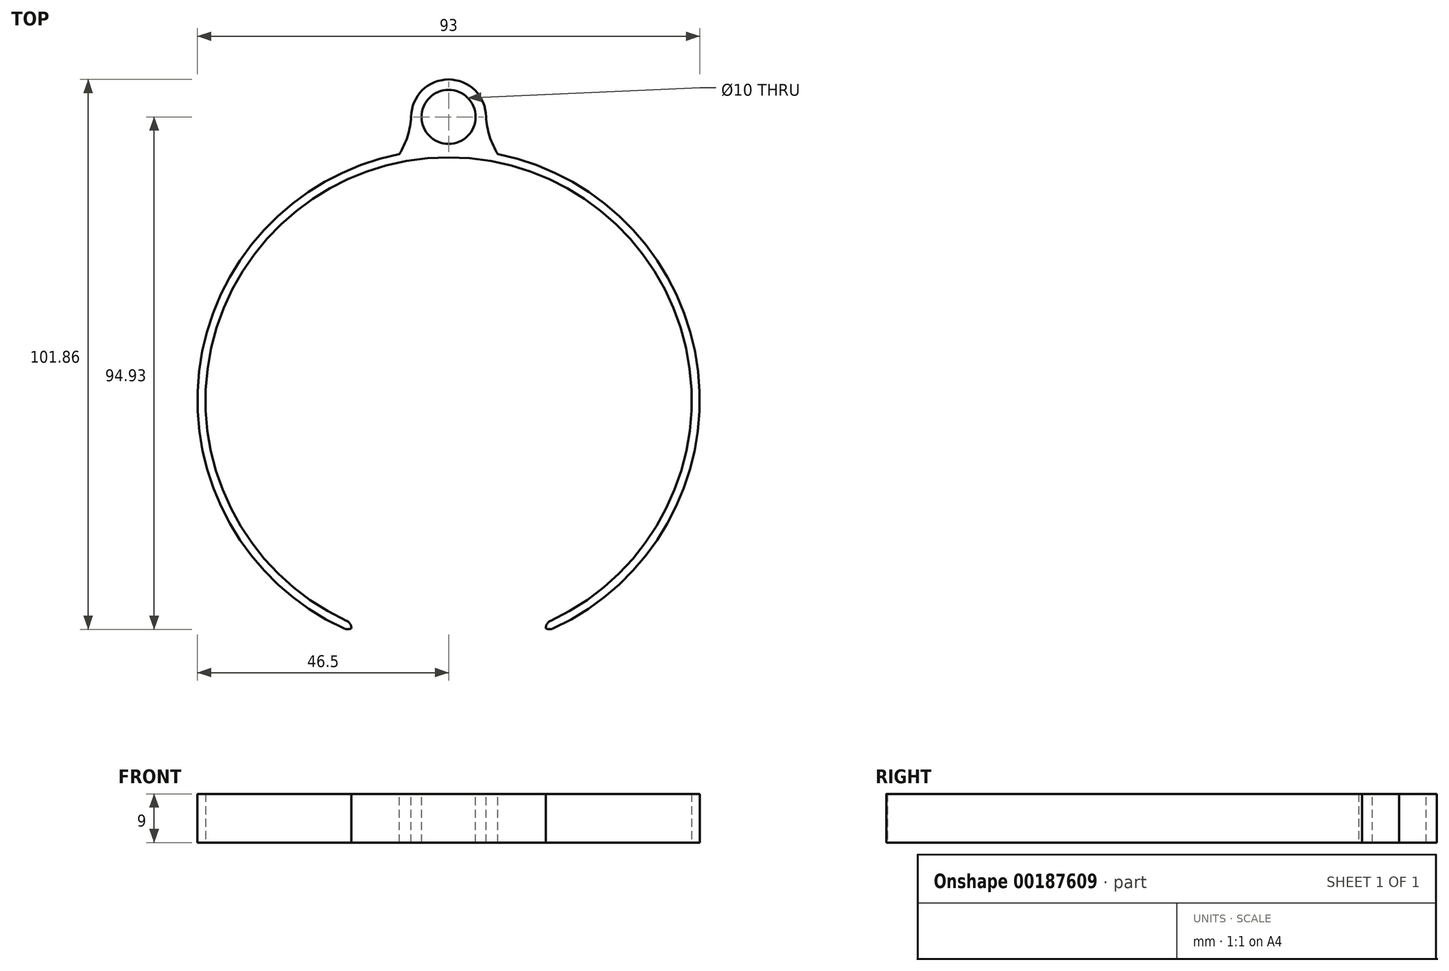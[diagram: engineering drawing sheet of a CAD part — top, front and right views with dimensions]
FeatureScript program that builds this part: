
annotation { "Feature Type Name" : "Feature", "Feature Type Description" : "" }
export const myFeature = defineFeature(function(context is Context, id is Id, definition is map)
    precondition{}
    {
        {
            var Q0;
            Q0=qCreatedBy(makeId("Top.planeOp"),FACE);
            var sketch = newSketch(context, id + "F0", { "sketchPlane" : qUnion([Q0])});
            skCircle(sketch, "E0", {"center": v(0, 0) * mm, "radius": 46.5 * mm});
            skCircle(sketch, "E1", {"center": v(0, 0) * mm, "radius": 45 * mm});
            skSolve(sketch);
        }
        {
            var Q0;
            Q0 = qSketchRegion(id + "F0", true);
            extrude(context, id + "F1", {"entities" : qUnion([Q0]), "depth" : 9 * mm});
        }
        {
            var Q0;
            Q0=makeQuery(id+"F1.opExtrude","CAP_FACE",FACE,{"disambiguationData":[OSD([sQuery(id+"F0.wireOp",EDGE,"E0"),sQuery(id+"F0.wireOp",EDGE,"E1")])],"isStart":false});
            var sketch = newSketch(context, id + "F2", { "sketchPlane" : qUnion([Q0])});
            skLineSegment(sketch, "E2", {"start": v(0, -21.51) * mm, "end": v(-51.57, -21.51) * mm});
            skLineSegment(sketch, "E3", {"start": v(-51.57, -21.51) * mm, "end": v(-51.57, -59.92) * mm});
            skLineSegment(sketch, "E4", {"start": v(-51.57, -59.92) * mm, "end": v(64.03, -57.77) * mm});
            skLineSegment(sketch, "E5", {"start": v(0, -21.51) * mm, "end": v(64.81, -21.51) * mm});
            skLineSegment(sketch, "E6", {"start": v(64.81, -21.51) * mm, "end": v(64.03, -57.77) * mm});
            skSolve(sketch);
        }
        {
            var Q0;
            Q0 = qSketchRegion(id + "F2", true);
            extrude(context, id + "F3", {"entities" : qUnion([Q0]), "operationType" : NewBodyOperationType.REMOVE, "oppositeDirection" : true, "depth" : 25 * mm});
        }
        {
            var Q0;
            Q0=makeQuery(id+"F1.opExtrude","CAP_FACE",FACE,{"disambiguationData":[OSD([sQuery(id+"F0.wireOp",EDGE,"E0"),sQuery(id+"F0.wireOp",EDGE,"E1")])],"isStart":false});
            var sketch = newSketch(context, id + "F4", { "sketchPlane" : qUnion([Q0])});
            skArc(sketch, "E7", {"start": v(-41.9, -20.16) * mm, "mid": v(-40.9, -20.5) * mm, "end": v(-40.55, -19.5) * mm});
            skLineSegment(sketch, "E8", {"start": v(-41.9, -20.16) * mm, "end": v(-43.43, -22.72) * mm});
            skLineSegment(sketch, "E9", {"start": v(-43.43, -22.72) * mm, "end": v(-36.35, -23.45) * mm});
            skLineSegment(sketch, "E10", {"start": v(-36.35, -23.45) * mm, "end": v(-40.55, -19.5) * mm});
            skLineSegment(sketch, "E11", {"start": v(0, 0) * mm, "end": v(0, -21.51) * mm});
            skArc(sketch, "E12.MirrorCS", {"start": v(41.9, -20.16) * mm, "mid": v(40.9, -20.5) * mm, "end": v(40.55, -19.5) * mm});
            skLineSegment(sketch, "E13.MirrorCS", {"start": v(36.35, -23.45) * mm, "end": v(40.55, -19.5) * mm});
            skLineSegment(sketch, "E14.MirrorCS", {"start": v(43.43, -22.72) * mm, "end": v(36.35, -23.45) * mm});
            skLineSegment(sketch, "E15.MirrorCS", {"start": v(41.9, -20.16) * mm, "end": v(43.43, -22.72) * mm});
            skSolve(sketch);
        }
        {
            var Q0;
            Q0 = qSketchRegion(id + "F4", true);
            extrude(context, id + "F5", {"entities" : qUnion([Q0]), "operationType" : NewBodyOperationType.REMOVE, "oppositeDirection" : true, "depth" : 25 * mm});
        }
        {
            var Q0;
            Q0=makeQuery(id+"F1.opExtrude","CAP_FACE",FACE,{"disambiguationData":[OSD([sQuery(id+"F0.wireOp",EDGE,"E0"),sQuery(id+"F0.wireOp",EDGE,"E1")])],"isStart":false});
            var sketch = newSketch(context, id + "F6", { "sketchPlane" : qUnion([Q0])});
            skLineSegment(sketch, "E16", {"start": v(0, 0) * mm, "end": v(0, 52.5) * mm});
            skCircle(sketch, "E17", {"center": v(0, 52.5) * mm, "radius": 5 * mm});
            skCircle(sketch, "E18", {"center": v(0, 52.5) * mm, "radius": 6.93 * mm});
            skSolve(sketch);
        }
        {
            var Q0;
            Q0 = qSketchRegion(id + "F6", true);
            extrude(context, id + "F7", {"entities" : qUnion([Q0]), "operationType" : NewBodyOperationType.ADD, "oppositeDirection" : true, "depth" : 9 * mm});
        }
        {
            var Q0;
            Q0=makeQuery(id+"F7.boolean.opBoolean","MERGE",FACE,{"derivedFrom":[makeQuery(id+"F1.opExtrude","CAP_FACE",FACE,{"disambiguationData":[OSD([sQuery(id+"F0.wireOp",EDGE,"E0"),sQuery(id+"F0.wireOp",EDGE,"E1")])],"isStart":false}),makeQuery(id+"F7.opExtrude","CAP_FACE",FACE,{"disambiguationData":[OSD([sQuery(id+"F6.wireOp",EDGE,"E17"),sQuery(id+"F6.wireOp",EDGE,"E18")])],"isStart":true})]});
            var sketch = newSketch(context, id + "F8", { "sketchPlane" : qUnion([Q0])});
            skArc(sketch, "E19", {"start": v(-9.12, 45.6) * mm, "mid": v(-7.6, 48.91) * mm, "end": v(-6.93, 52.5) * mm});
            skArc(sketch, "E20.MirrorCS", {"start": v(9.12, 45.6) * mm, "mid": v(7.6, 48.91) * mm, "end": v(6.93, 52.5) * mm});
            skArc(sketch, "E21", {"start": v(9.12, 45.6) * mm, "mid": v(0, 45.6) * mm, "end": v(-9.12, 45.6) * mm});
            skArc(sketch, "E22", {"start": v(-6.93, 52.5) * mm, "mid": v(0, 47) * mm, "end": v(6.93, 52.5) * mm});
            skSolve(sketch);
        }
        {
            var Q0;
            Q0 = qSketchRegion(id + "F8", true);
            extrude(context, id + "F9", {"entities" : qUnion([Q0]), "operationType" : NewBodyOperationType.ADD, "oppositeDirection" : true, "depth" : 9 * mm});
        }
        {
            var Q0;
            Q0=makeQuery(id+"F9.boolean.opBoolean","MERGE",FACE,{"derivedFrom":[makeQuery(id+"F7.boolean.opBoolean","MERGE",FACE,{"derivedFrom":[makeQuery(id+"F1.opExtrude","CAP_FACE",FACE,{"disambiguationData":[OSD([sQuery(id+"F0.wireOp",EDGE,"E0"),sQuery(id+"F0.wireOp",EDGE,"E1")])],"isStart":false}),makeQuery(id+"F7.opExtrude","CAP_FACE",FACE,{"disambiguationData":[OSD([sQuery(id+"F6.wireOp",EDGE,"E17"),sQuery(id+"F6.wireOp",EDGE,"E18")])],"isStart":true})]}),makeQuery(id+"F9.opExtrude","CAP_FACE",FACE,{"disambiguationData":[OSD([sQuery(id+"F8.wireOp",EDGE,"E19"),sQuery(id+"F8.wireOp",EDGE,"E20.MirrorCS"),sQuery(id+"F8.wireOp",EDGE,"E21"),sQuery(id+"F8.wireOp",EDGE,"E22")])],"isStart":true})]});
            var sketch = newSketch(context, id + "F10", { "sketchPlane" : qUnion([Q0])});
            skArc(sketch, "E23", {"start": v(-46.35, 3.8) * mm, "mid": v(-42.8, -9.52) * mm, "end": v(-33.84, -20) * mm});
            skArc(sketch, "E24", {"start": v(-44.83, 3.9) * mm, "mid": v(-41.28, -9.32) * mm, "end": v(-32.15, -19.5) * mm});
            skArc(sketch, "E25", {"start": v(-33.84, -20) * mm, "mid": v(-32.86, -20.21) * mm, "end": v(-32.15, -19.5) * mm});
            skLineSegment(sketch, "E26", {"start": v(-46.35, 3.8) * mm, "end": v(-44.83, 3.9) * mm});
            skLineSegment(sketch, "E27", {"start": v(0, 0) * mm, "end": v(0, 28.55) * mm});
            skLineSegment(sketch, "E28.MirrorCS", {"start": v(46.35, 3.8) * mm, "end": v(44.83, 3.9) * mm});
            skArc(sketch, "E29.MirrorCS", {"start": v(46.35, 3.8) * mm, "mid": v(42.8, -9.52) * mm, "end": v(33.84, -20) * mm});
            skArc(sketch, "E30.MirrorCS", {"start": v(44.83, 3.9) * mm, "mid": v(41.28, -9.32) * mm, "end": v(32.15, -19.5) * mm});
            skArc(sketch, "E31.MirrorCS", {"start": v(33.84, -20) * mm, "mid": v(32.86, -20.21) * mm, "end": v(32.15, -19.5) * mm});
            skSolve(sketch);
        }
        {
            var Q0;
            Q0 = qSketchRegion(id + "F10", true);
            extrude(context, id + "F11", {"entities" : qUnion([Q0]), "operationType" : NewBodyOperationType.ADD, "oppositeDirection" : true, "depth" : 9 * mm});
        }
        {
            var Q0;
            Q0=makeQuery(id+"F11.boolean.opBoolean","MERGE",FACE,{"derivedFrom":[makeQuery(id+"F9.boolean.opBoolean","MERGE",FACE,{"derivedFrom":[makeQuery(id+"F7.boolean.opBoolean","MERGE",FACE,{"derivedFrom":[makeQuery(id+"F1.opExtrude","CAP_FACE",FACE,{"disambiguationData":[OSD([sQuery(id+"F0.wireOp",EDGE,"E0"),sQuery(id+"F0.wireOp",EDGE,"E1")])],"isStart":false}),makeQuery(id+"F7.opExtrude","CAP_FACE",FACE,{"disambiguationData":[OSD([sQuery(id+"F6.wireOp",EDGE,"E17"),sQuery(id+"F6.wireOp",EDGE,"E18")])],"isStart":true})]}),makeQuery(id+"F9.opExtrude","CAP_FACE",FACE,{"disambiguationData":[OSD([sQuery(id+"F8.wireOp",EDGE,"E19"),sQuery(id+"F8.wireOp",EDGE,"E20.MirrorCS"),sQuery(id+"F8.wireOp",EDGE,"E21"),sQuery(id+"F8.wireOp",EDGE,"E22")])],"isStart":true})]}),makeQuery(id+"F11.opExtrude","CAP_FACE",FACE,{"disambiguationData":[OSD([sQuery(id+"F10.wireOp",EDGE,"E23"),sQuery(id+"F10.wireOp",EDGE,"E24"),sQuery(id+"F10.wireOp",EDGE,"E25"),sQuery(id+"F10.wireOp",EDGE,"E26")])],"isStart":true}),makeQuery(id+"F11.opExtrude","CAP_FACE",FACE,{"disambiguationData":[OSD([sQuery(id+"F10.wireOp",EDGE,"E28.MirrorCS"),sQuery(id+"F10.wireOp",EDGE,"E29.MirrorCS"),sQuery(id+"F10.wireOp",EDGE,"E30.MirrorCS"),sQuery(id+"F10.wireOp",EDGE,"E31.MirrorCS")])],"isStart":true})]});
            var sketch = newSketch(context, id + "F12", { "sketchPlane" : qUnion([Q0])});
            skArc(sketch, "E32", {"start": v(-46.38, 3.36) * mm, "mid": v(-45.83, -0.9) * mm, "end": v(-44.72, -5.04) * mm});
            skLineSegment(sketch, "E33", {"start": v(-46.38, 3.36) * mm, "end": v(-53.97, -20.4) * mm});
            skLineSegment(sketch, "E34", {"start": v(-53.97, -20.4) * mm, "end": v(-39.63, -26.7) * mm});
            skLineSegment(sketch, "E35", {"start": v(-39.63, -26.7) * mm, "end": v(-35.97, -21.97) * mm});
            skLineSegment(sketch, "E36", {"start": v(-35.97, -21.97) * mm, "end": v(-43.3, -10.16) * mm});
            skLineSegment(sketch, "E37", {"start": v(-43.3, -10.16) * mm, "end": v(-44.72, -5.04) * mm});
            skLineSegment(sketch, "E38.MirrorCS", {"start": v(46.38, 3.36) * mm, "end": v(53.97, -20.4) * mm});
            skLineSegment(sketch, "E39.MirrorCS", {"start": v(53.97, -20.4) * mm, "end": v(39.63, -26.7) * mm});
            skLineSegment(sketch, "E40.MirrorCS", {"start": v(39.63, -26.7) * mm, "end": v(35.97, -21.97) * mm});
            skLineSegment(sketch, "E41.MirrorCS", {"start": v(35.97, -21.97) * mm, "end": v(43.3, -10.16) * mm});
            skArc(sketch, "E42.MirrorCS", {"start": v(46.38, 3.36) * mm, "mid": v(45.83, -0.9) * mm, "end": v(44.72, -5.04) * mm});
            skLineSegment(sketch, "E43.MirrorCS", {"start": v(43.3, -10.16) * mm, "end": v(44.72, -5.04) * mm});
            skSolve(sketch);
        }
        {
            var Q0;
            Q0 = qSketchRegion(id + "F12", true);
            extrude(context, id + "F13", {"entities" : qUnion([Q0]), "operationType" : NewBodyOperationType.REMOVE, "oppositeDirection" : true, "depth" : 25 * mm});
        }
        {
            var Q0;
            Q0=makeQuery(id+"F11.boolean.opBoolean","MERGE",FACE,{"derivedFrom":[makeQuery(id+"F9.boolean.opBoolean","MERGE",FACE,{"derivedFrom":[makeQuery(id+"F7.boolean.opBoolean","MERGE",FACE,{"derivedFrom":[makeQuery(id+"F1.opExtrude","CAP_FACE",FACE,{"disambiguationData":[OSD([sQuery(id+"F0.wireOp",EDGE,"E0"),sQuery(id+"F0.wireOp",EDGE,"E1")])],"isStart":false}),makeQuery(id+"F7.opExtrude","CAP_FACE",FACE,{"disambiguationData":[OSD([sQuery(id+"F6.wireOp",EDGE,"E17"),sQuery(id+"F6.wireOp",EDGE,"E18")])],"isStart":true})]}),makeQuery(id+"F9.opExtrude","CAP_FACE",FACE,{"disambiguationData":[OSD([sQuery(id+"F8.wireOp",EDGE,"E19"),sQuery(id+"F8.wireOp",EDGE,"E20.MirrorCS"),sQuery(id+"F8.wireOp",EDGE,"E21"),sQuery(id+"F8.wireOp",EDGE,"E22")])],"isStart":true})]}),makeQuery(id+"F11.opExtrude","CAP_FACE",FACE,{"disambiguationData":[OSD([sQuery(id+"F10.wireOp",EDGE,"E23"),sQuery(id+"F10.wireOp",EDGE,"E24"),sQuery(id+"F10.wireOp",EDGE,"E25"),sQuery(id+"F10.wireOp",EDGE,"E26")])],"isStart":true}),makeQuery(id+"F11.opExtrude","CAP_FACE",FACE,{"disambiguationData":[OSD([sQuery(id+"F10.wireOp",EDGE,"E28.MirrorCS"),sQuery(id+"F10.wireOp",EDGE,"E29.MirrorCS"),sQuery(id+"F10.wireOp",EDGE,"E30.MirrorCS"),sQuery(id+"F10.wireOp",EDGE,"E31.MirrorCS")])],"isStart":true})]});
            var sketch = newSketch(context, id + "F14", { "sketchPlane" : qUnion([Q0])});
            skArc(sketch, "E44", {"start": v(-45.86, 7.72) * mm, "mid": v(-46.14, 3.23) * mm, "end": v(-45.76, -1.25) * mm});
            skArc(sketch, "E45", {"start": v(-45.86, 7.72) * mm, "mid": v(-48.53, 3.2) * mm, "end": v(-45.76, -1.25) * mm});
            skArc(sketch, "E46.MirrorCS", {"start": v(45.86, 7.72) * mm, "mid": v(48.53, 3.2) * mm, "end": v(45.76, -1.25) * mm});
            skArc(sketch, "E47.MirrorCS", {"start": v(45.86, 7.72) * mm, "mid": v(46.14, 3.23) * mm, "end": v(45.76, -1.25) * mm});
            skSolve(sketch);
        }
        {
            var Q0;
            Q0 = qSketchRegion(id + "F14", true);
            extrude(context, id + "F15", {"entities" : qUnion([Q0]), "operationType" : NewBodyOperationType.REMOVE, "oppositeDirection" : true, "depth" : 25 * mm});
        }
        {
            var Q0;
            Q0=makeQuery(id+"F11.boolean.opBoolean","MERGE",FACE,{"derivedFrom":[makeQuery(id+"F9.boolean.opBoolean","MERGE",FACE,{"derivedFrom":[makeQuery(id+"F7.boolean.opBoolean","MERGE",FACE,{"derivedFrom":[makeQuery(id+"F1.opExtrude","CAP_FACE",FACE,{"disambiguationData":[OSD([sQuery(id+"F0.wireOp",EDGE,"E0"),sQuery(id+"F0.wireOp",EDGE,"E1")])],"isStart":false}),makeQuery(id+"F7.opExtrude","CAP_FACE",FACE,{"disambiguationData":[OSD([sQuery(id+"F6.wireOp",EDGE,"E17"),sQuery(id+"F6.wireOp",EDGE,"E18")])],"isStart":true})]}),makeQuery(id+"F9.opExtrude","CAP_FACE",FACE,{"disambiguationData":[OSD([sQuery(id+"F8.wireOp",EDGE,"E19"),sQuery(id+"F8.wireOp",EDGE,"E20.MirrorCS"),sQuery(id+"F8.wireOp",EDGE,"E21"),sQuery(id+"F8.wireOp",EDGE,"E22")])],"isStart":true})]}),makeQuery(id+"F11.opExtrude","CAP_FACE",FACE,{"disambiguationData":[OSD([sQuery(id+"F10.wireOp",EDGE,"E23"),sQuery(id+"F10.wireOp",EDGE,"E24"),sQuery(id+"F10.wireOp",EDGE,"E25"),sQuery(id+"F10.wireOp",EDGE,"E26")])],"isStart":true}),makeQuery(id+"F11.opExtrude","CAP_FACE",FACE,{"disambiguationData":[OSD([sQuery(id+"F10.wireOp",EDGE,"E28.MirrorCS"),sQuery(id+"F10.wireOp",EDGE,"E29.MirrorCS"),sQuery(id+"F10.wireOp",EDGE,"E30.MirrorCS"),sQuery(id+"F10.wireOp",EDGE,"E31.MirrorCS")])],"isStart":true})]});
            var sketch = newSketch(context, id + "F16", { "sketchPlane" : qUnion([Q0])});
            skArc(sketch, "E48", {"start": v(9.12, 45.6) * mm, "mid": v(0, 46.5) * mm, "end": v(-9.12, 45.6) * mm});
            skArc(sketch, "E49", {"start": v(-9.12, 45.6) * mm, "mid": v(0, -46.5) * mm, "end": v(9.12, 45.6) * mm});
            skCircle(sketch, "E50", {"center": v(0, 0) * mm, "radius": 45 * mm});
            skSolve(sketch);
        }
        {
            var Q0;
            Q0 = qSketchRegion(id + "F16", true);
            extrude(context, id + "F17", {"entities" : qUnion([Q0]), "operationType" : NewBodyOperationType.ADD, "oppositeDirection" : true, "depth" : 9 * mm});
        }
        {
            var Q0;
            Q0=makeQuery(id+"F17.boolean.opBoolean","MERGE",FACE,{"derivedFrom":[makeQuery(id+"F11.boolean.opBoolean","MERGE",FACE,{"derivedFrom":[makeQuery(id+"F9.boolean.opBoolean","MERGE",FACE,{"derivedFrom":[makeQuery(id+"F7.boolean.opBoolean","MERGE",FACE,{"derivedFrom":[makeQuery(id+"F1.opExtrude","CAP_FACE",FACE,{"disambiguationData":[OSD([sQuery(id+"F0.wireOp",EDGE,"E0"),sQuery(id+"F0.wireOp",EDGE,"E1")])],"isStart":false}),makeQuery(id+"F7.opExtrude","CAP_FACE",FACE,{"disambiguationData":[OSD([sQuery(id+"F6.wireOp",EDGE,"E17"),sQuery(id+"F6.wireOp",EDGE,"E18")])],"isStart":true})]}),makeQuery(id+"F9.opExtrude","CAP_FACE",FACE,{"disambiguationData":[OSD([sQuery(id+"F8.wireOp",EDGE,"E19"),sQuery(id+"F8.wireOp",EDGE,"E20.MirrorCS"),sQuery(id+"F8.wireOp",EDGE,"E21"),sQuery(id+"F8.wireOp",EDGE,"E22")])],"isStart":true})]}),makeQuery(id+"F11.opExtrude","CAP_FACE",FACE,{"disambiguationData":[OSD([sQuery(id+"F10.wireOp",EDGE,"E23"),sQuery(id+"F10.wireOp",EDGE,"E24"),sQuery(id+"F10.wireOp",EDGE,"E25"),sQuery(id+"F10.wireOp",EDGE,"E26")])],"isStart":true}),makeQuery(id+"F11.opExtrude","CAP_FACE",FACE,{"disambiguationData":[OSD([sQuery(id+"F10.wireOp",EDGE,"E28.MirrorCS"),sQuery(id+"F10.wireOp",EDGE,"E29.MirrorCS"),sQuery(id+"F10.wireOp",EDGE,"E30.MirrorCS"),sQuery(id+"F10.wireOp",EDGE,"E31.MirrorCS")])],"isStart":true})]}),makeQuery(id+"F17.opExtrude","CAP_FACE",FACE,{"disambiguationData":[OSD([sQuery(id+"F16.wireOp",EDGE,"E48"),sQuery(id+"F16.wireOp",EDGE,"E49"),sQuery(id+"F16.wireOp",EDGE,"E50")])],"isStart":true})]});
            var sketch = newSketch(context, id + "F18", { "sketchPlane" : qUnion([Q0])});
            skCircle(sketch, "E51", {"center": v(0, 0) * mm, "radius": 45 * mm});
            skSolve(sketch);
        }
        {
            var Q0;
            Q0 = qSketchRegion(id + "F18", true);
            extrude(context, id + "F19", {"entities" : qUnion([Q0]), "operationType" : NewBodyOperationType.REMOVE, "oppositeDirection" : true, "depth" : 25 * mm});
        }
        {
            var Q0;
            Q0=makeQuery(id+"F17.boolean.opBoolean","MERGE",FACE,{"derivedFrom":[makeQuery(id+"F11.boolean.opBoolean","MERGE",FACE,{"derivedFrom":[makeQuery(id+"F9.boolean.opBoolean","MERGE",FACE,{"derivedFrom":[makeQuery(id+"F7.boolean.opBoolean","MERGE",FACE,{"derivedFrom":[makeQuery(id+"F1.opExtrude","CAP_FACE",FACE,{"disambiguationData":[OSD([sQuery(id+"F0.wireOp",EDGE,"E0"),sQuery(id+"F0.wireOp",EDGE,"E1")])],"isStart":false}),makeQuery(id+"F7.opExtrude","CAP_FACE",FACE,{"disambiguationData":[OSD([sQuery(id+"F6.wireOp",EDGE,"E17"),sQuery(id+"F6.wireOp",EDGE,"E18")])],"isStart":true})]}),makeQuery(id+"F9.opExtrude","CAP_FACE",FACE,{"disambiguationData":[OSD([sQuery(id+"F8.wireOp",EDGE,"E19"),sQuery(id+"F8.wireOp",EDGE,"E20.MirrorCS"),sQuery(id+"F8.wireOp",EDGE,"E21"),sQuery(id+"F8.wireOp",EDGE,"E22")])],"isStart":true})]}),makeQuery(id+"F11.opExtrude","CAP_FACE",FACE,{"disambiguationData":[OSD([sQuery(id+"F10.wireOp",EDGE,"E23"),sQuery(id+"F10.wireOp",EDGE,"E24"),sQuery(id+"F10.wireOp",EDGE,"E25"),sQuery(id+"F10.wireOp",EDGE,"E26")])],"isStart":true}),makeQuery(id+"F11.opExtrude","CAP_FACE",FACE,{"disambiguationData":[OSD([sQuery(id+"F10.wireOp",EDGE,"E28.MirrorCS"),sQuery(id+"F10.wireOp",EDGE,"E29.MirrorCS"),sQuery(id+"F10.wireOp",EDGE,"E30.MirrorCS"),sQuery(id+"F10.wireOp",EDGE,"E31.MirrorCS")])],"isStart":true})]}),makeQuery(id+"F17.opExtrude","CAP_FACE",FACE,{"disambiguationData":[OSD([sQuery(id+"F16.wireOp",EDGE,"E48"),sQuery(id+"F16.wireOp",EDGE,"E49"),sQuery(id+"F16.wireOp",EDGE,"E50")])],"isStart":true})]});
            var sketch = newSketch(context, id + "F20", { "sketchPlane" : qUnion([Q0])});
            skLineSegment(sketch, "E52", {"start": v(0, 0) * mm, "end": v(18, 0) * mm});
            skLineSegment(sketch, "E53", {"start": v(0, 0) * mm, "end": v(-18, 0) * mm});
            skLineSegment(sketch, "E54", {"start": v(-18, 0) * mm, "end": v(-18, -69.98) * mm});
            skLineSegment(sketch, "E55", {"start": v(18, 0) * mm, "end": v(18, -69.4) * mm});
            skLineSegment(sketch, "E56", {"start": v(18, -69.4) * mm, "end": v(-18, -69.98) * mm});
            skSolve(sketch);
        }
        {
            var Q0;
            Q0 = qSketchRegion(id + "F20", true);
            extrude(context, id + "F21", {"entities" : qUnion([Q0]), "operationType" : NewBodyOperationType.REMOVE, "oppositeDirection" : true, "depth" : 25 * mm});
        }
        {
            var Q0;
            {var subQ4=sQuery(id+"F10.wireOp",EDGE,"E24");var subQ12=sQuery(id+"F0.wireOp",EDGE,"E1");Q0=makeQuery(id+"F21.boolean.opBoolean","INTERSECT",EDGE,{"derivedFrom":[makeQuery(id+"F19.boolean.opBoolean","MERGE",FACE,{"derivedFrom":[makeQuery(id+"F11.boolean.opBoolean","SPLIT",FACE,{"disambiguationData":[TD([makeQuery(id+"F11.opExtrude","SWEPT_FACE",FACE,{"disambiguationData":[OSD([subQ4])]})])],"derivedFrom":makeQuery(id+"F1.opExtrude","SWEPT_FACE",FACE,{"disambiguationData":[OSD([subQ12])]})}),makeQuery(id+"F17.opExtrude","SWEPT_FACE",FACE,{"disambiguationData":[OSD([sQuery(id+"F16.wireOp",EDGE,"E50")])]}),makeQuery(id+"F19.opExtrude","SWEPT_FACE",FACE,{"disambiguationData":[OSD([sQuery(id+"F18.wireOp",EDGE,"E51")])]})]}),makeQuery(id+"F21.opExtrude","SWEPT_FACE",FACE,{"disambiguationData":[OSD([sQuery(id+"F20.wireOp",EDGE,"E54")])]})]});}
            var Q1;
            {var subQ4=sQuery(id+"F10.wireOp",EDGE,"E24");var subQ12=sQuery(id+"F0.wireOp",EDGE,"E1");Q1=makeQuery(id+"F21.boolean.opBoolean","INTERSECT",EDGE,{"derivedFrom":[makeQuery(id+"F19.boolean.opBoolean","MERGE",FACE,{"derivedFrom":[makeQuery(id+"F11.boolean.opBoolean","SPLIT",FACE,{"disambiguationData":[TD([makeQuery(id+"F11.opExtrude","SWEPT_FACE",FACE,{"disambiguationData":[OSD([subQ4])]})])],"derivedFrom":makeQuery(id+"F1.opExtrude","SWEPT_FACE",FACE,{"disambiguationData":[OSD([subQ12])]})}),makeQuery(id+"F17.opExtrude","SWEPT_FACE",FACE,{"disambiguationData":[OSD([sQuery(id+"F16.wireOp",EDGE,"E50")])]}),makeQuery(id+"F19.opExtrude","SWEPT_FACE",FACE,{"disambiguationData":[OSD([sQuery(id+"F18.wireOp",EDGE,"E51")])]})]}),makeQuery(id+"F21.opExtrude","SWEPT_FACE",FACE,{"disambiguationData":[OSD([sQuery(id+"F20.wireOp",EDGE,"E55")])]})]});}
            fillet(context, id + "F22", {"entities" : qUnion([Q0, Q1]), "radius" : 1.55 * mm, "tangentPropagation" : true, "allowEdgeOverflow" : false});
        }
        {
            var Q0;
            {var subQ4=sQuery(id+"F0.wireOp",EDGE,"E0");var subQ9=makeQuery(id+"F1.opExtrude","SWEPT_FACE",FACE,{"disambiguationData":[OSD([subQ4])]});Q0=makeQuery(id+"F21.boolean.opBoolean","INTERSECT",EDGE,{"derivedFrom":[makeQuery(id+"F17.boolean.opBoolean","MERGE",FACE,{"derivedFrom":[makeQuery(id+"F7.boolean.opBoolean","SPLIT",FACE,{"disambiguationData":[TD([makeQuery(id+"F5.boolean.opBoolean","COPY",FACE,{"derivedFrom":makeQuery(id+"F5.opExtrude","SWEPT_FACE",FACE,{"disambiguationData":[OSD([sQuery(id+"F4.wireOp",EDGE,"E7")])]})})])],"derivedFrom":subQ9}),makeQuery(id+"F7.boolean.opBoolean","SPLIT",FACE,{"disambiguationData":[TD([makeQuery(id+"F5.boolean.opBoolean","COPY",FACE,{"derivedFrom":makeQuery(id+"F5.opExtrude","SWEPT_FACE",FACE,{"disambiguationData":[OSD([sQuery(id+"F4.wireOp",EDGE,"E12.MirrorCS")])]})})])],"derivedFrom":subQ9}),makeQuery(id+"F17.opExtrude","SWEPT_FACE",FACE,{"disambiguationData":[OSD([sQuery(id+"F16.wireOp",EDGE,"E48"),sQuery(id+"F16.wireOp",EDGE,"E49")])]})]}),makeQuery(id+"F21.opExtrude","SWEPT_FACE",FACE,{"disambiguationData":[OSD([sQuery(id+"F20.wireOp",EDGE,"E55")])]})]});}
            fillet(context, id + "F23", {"entities" : qUnion([Q0]), "radius" : 1.5 * mm, "tangentPropagation" : true, "allowEdgeOverflow" : false});
        }
        {
            var Q0;
            {var subQ4=sQuery(id+"F0.wireOp",EDGE,"E0");var subQ9=makeQuery(id+"F1.opExtrude","SWEPT_FACE",FACE,{"disambiguationData":[OSD([subQ4])]});Q0=makeQuery(id+"F21.boolean.opBoolean","INTERSECT",EDGE,{"derivedFrom":[makeQuery(id+"F17.boolean.opBoolean","MERGE",FACE,{"derivedFrom":[makeQuery(id+"F7.boolean.opBoolean","SPLIT",FACE,{"disambiguationData":[TD([makeQuery(id+"F5.boolean.opBoolean","COPY",FACE,{"derivedFrom":makeQuery(id+"F5.opExtrude","SWEPT_FACE",FACE,{"disambiguationData":[OSD([sQuery(id+"F4.wireOp",EDGE,"E7")])]})})])],"derivedFrom":subQ9}),makeQuery(id+"F7.boolean.opBoolean","SPLIT",FACE,{"disambiguationData":[TD([makeQuery(id+"F5.boolean.opBoolean","COPY",FACE,{"derivedFrom":makeQuery(id+"F5.opExtrude","SWEPT_FACE",FACE,{"disambiguationData":[OSD([sQuery(id+"F4.wireOp",EDGE,"E12.MirrorCS")])]})})])],"derivedFrom":subQ9}),makeQuery(id+"F17.opExtrude","SWEPT_FACE",FACE,{"disambiguationData":[OSD([sQuery(id+"F16.wireOp",EDGE,"E48"),sQuery(id+"F16.wireOp",EDGE,"E49")])]})]}),makeQuery(id+"F21.opExtrude","SWEPT_FACE",FACE,{"disambiguationData":[OSD([sQuery(id+"F20.wireOp",EDGE,"E54")])]})]});}
            fillet(context, id + "F24", {"entities" : qUnion([Q0]), "radius" : 1.5 * mm, "tangentPropagation" : true, "allowEdgeOverflow" : false});
        }
    });
